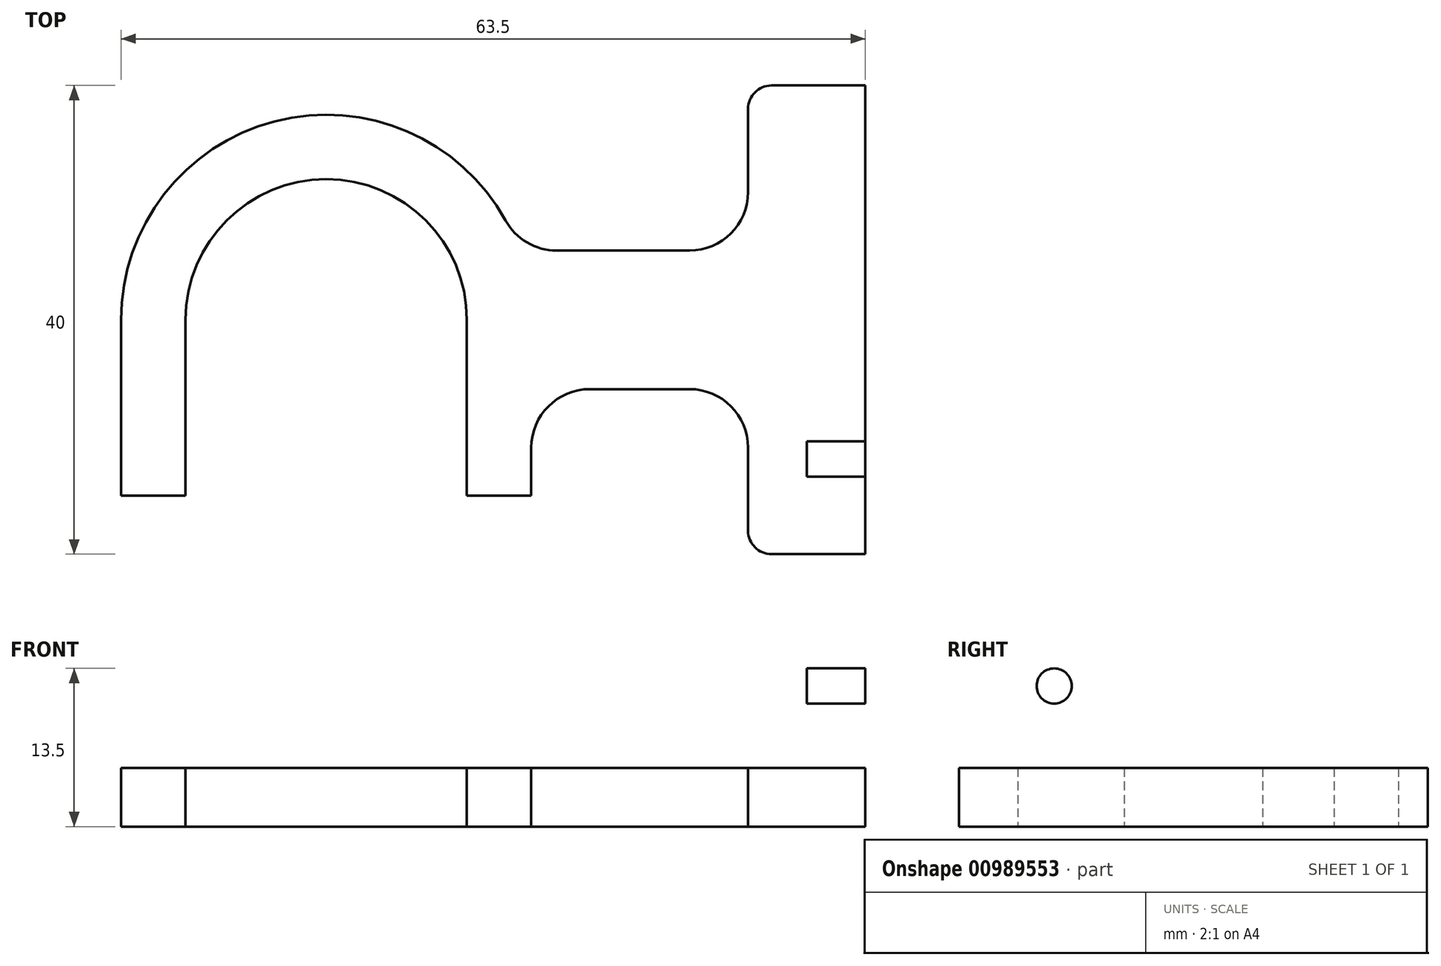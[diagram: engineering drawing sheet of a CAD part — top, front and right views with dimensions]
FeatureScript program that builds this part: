
annotation { "Feature Type Name" : "Feature", "Feature Type Description" : "" }
export const myFeature = defineFeature(function(context is Context, id is Id, definition is map)
    precondition{}
    {
        {
            var Q0;
            Q0=qCreatedBy(makeId("Top.planeOp"),FACE);
            var sketch = newSketch(context, id + "F0", { "sketchPlane" : qUnion([Q0])});
            skLineSegment(sketch, "E0", {"start": v(12, 0) * mm, "end": v(46, 0) * mm, "construction": true});
            skLineSegment(sketch, "E1", {"start": v(36, 10.91) * mm, "end": v(36, 18) * mm});
            skLineSegment(sketch, "E2", {"start": v(38, 20) * mm, "end": v(46, 20) * mm});
            skLineSegment(sketch, "E3", {"start": v(46, 20) * mm, "end": v(46, 0) * mm});
            skLineSegment(sketch, "E4.MirrorCS", {"start": v(36, -10.91) * mm, "end": v(36, -18) * mm});
            skLineSegment(sketch, "E5.MirrorCS", {"start": v(38, -20) * mm, "end": v(46, -20) * mm});
            skLineSegment(sketch, "E6.MirrorCS", {"start": v(46, -20) * mm, "end": v(46, 0) * mm});
            skPoint(sketch, "E7.visualSharp", {"position": v(36, 5.91) * mm});
            skArc(sketch, "E7.filletArc", {"start": v(31, 5.91) * mm, "mid": v(34.54, 7.37) * mm, "end": v(36, 10.91) * mm});
            skArc(sketch, "E8.MirrorCS", {"start": v(31, -5.91) * mm, "mid": v(34.54, -7.37) * mm, "end": v(36, -10.91) * mm});
            skPoint(sketch, "E9.orphan", {"position": v(36, -5.91) * mm});
            skPoint(sketch, "E10.visualSharp", {"position": v(36, 20) * mm});
            skArc(sketch, "E10.filletArc", {"start": v(38, 20) * mm, "mid": v(36.59, 19.41) * mm, "end": v(36, 18) * mm});
            skPoint(sketch, "E11.visualSharp", {"position": v(36, -20) * mm});
            skArc(sketch, "E11.filletArc", {"start": v(36, -18) * mm, "mid": v(36.59, -19.41) * mm, "end": v(38, -20) * mm});
            skArc(sketch, "E12", {"start": v(12, 0) * mm, "mid": v(0, 12) * mm, "end": v(-12, 0) * mm});
            skArc(sketch, "E13", {"start": v(15.3, 8.49) * mm, "mid": v(-4.38, 16.94) * mm, "end": v(-17.5, 0) * mm});
            skLineSegment(sketch, "E14", {"start": v(31, 5.91) * mm, "end": v(19.68, 5.91) * mm});
            skLineSegment(sketch, "E15", {"start": v(31, -5.91) * mm, "end": v(22.5, -5.91) * mm});
            skLineSegment(sketch, "E16", {"start": v(12, 0) * mm, "end": v(12, -15) * mm});
            skLineSegment(sketch, "E17", {"start": v(-12, 0) * mm, "end": v(-12, -15) * mm});
            skLineSegment(sketch, "E18", {"start": v(-17.5, 0) * mm, "end": v(-17.5, -15) * mm});
            skLineSegment(sketch, "E19", {"start": v(17.5, -10.91) * mm, "end": v(17.5, -15) * mm});
            skLineSegment(sketch, "E20", {"start": v(12, -15) * mm, "end": v(17.5, -15) * mm});
            skLineSegment(sketch, "E21.trimOffspring", {"start": v(-12, -15) * mm, "end": v(-17.5, -15) * mm});
            skPoint(sketch, "E22.newPointB", {"position": v(17.5, 0) * mm});
            skArc(sketch, "E22.filletArc", {"start": v(22.5, -5.91) * mm, "mid": v(18.96, -7.37) * mm, "end": v(17.5, -10.91) * mm});
            skArc(sketch, "E23.filletArc", {"start": v(15.3, 8.49) * mm, "mid": v(17.14, 6.6) * mm, "end": v(19.68, 5.91) * mm});
            skSolve(sketch);
        }
        {
            var Q0;
            Q0=makeQuery(id+"F0.imprint","IMPRINT",FACE,{"disambiguationData":[TD([[makeQuery(id+"F0.imprint","IMPRINT",EDGE,{"derivedFrom":sQuery(id+"F0.wireOp",EDGE,"E1")}),-1.0]])]});
            extrude(context, id + "F1", {"entities" : qUnion([Q0]), "depth" : 5 * mm, "offsetDistance" : 25 * mm});
        }
        {
            var Q0;
            Q0=makeQuery(id+"F1.opExtrude","CAP_FACE",FACE,{"disambiguationData":[OSD([sQuery(id+"F0.wireOp",EDGE,"8GoCG5PU-HMSi-upqe-bQzh-JhpqWkjr83KI"),sQuery(id+"F0.wireOp",EDGE,"6tSREIWh-PCzu-5Fpg-hHSP-1HsGlxRufVVe"),sQuery(id+"F0.wireOp",EDGE,"E1"),sQuery(id+"F0.wireOp",EDGE,"E2"),sQuery(id+"F0.wireOp",EDGE,"E3"),sQuery(id+"F0.wireOp",EDGE,"6c7d7d15-5ab0-4980-99c8-1d9f464195fa0.MirrorCS"),sQuery(id+"F0.wireOp",EDGE,"E4.MirrorCS"),sQuery(id+"F0.wireOp",EDGE,"E5.MirrorCS"),sQuery(id+"F0.wireOp",EDGE,"E6.MirrorCS"),sQuery(id+"F0.wireOp",EDGE,"4b4e5443-fceb-4e8f-891c-267329df489d.filletArc"),sQuery(id+"F0.wireOp",EDGE,"E7.filletArc"),sQuery(id+"F0.wireOp",EDGE,"f6371bfa-6fd3-4287-8063-b7b2dde3479b0.MirrorCS"),sQuery(id+"F0.wireOp",EDGE,"E8.MirrorCS"),sQuery(id+"F0.wireOp",EDGE,"E10.filletArc"),sQuery(id+"F0.wireOp",EDGE,"E11.filletArc"),sQuery(id+"F0.wireOp",EDGE,"j99mnrsG-8fU8-ieAR-sIlP-IDkVLY8FqcVX"),sQuery(id+"F0.wireOp",EDGE,"e8211b01-7222-4893-8a72-a379b8b1651b.filletArc"),sQuery(id+"F0.wireOp",EDGE,"3d5b7bb5-eaf6-46b8-ad04-4672c3b9e5740.MirrorCS"),sQuery(id+"F0.wireOp",EDGE,"d1ffaaae-a754-4f0a-98e9-f6a03d5876740.MirrorCS"),sQuery(id+"F0.wireOp",EDGE,"7b9e766f-8db9-407e-a57f-f296288e7c8c.trimOffspring"),sQuery(id+"F0.wireOp",EDGE,"2bcb20b7-2aad-45c3-abd7-b2b32656667b.trimOffspring")])],"isStart":false});
            var sketch = newSketch(context, id + "F2", { "sketchPlane" : qUnion([Q0])});
            skLineSegment(sketch, "E24.bottom", {"start": v(46, 20) * mm, "end": v(41, 20) * mm});
            skLineSegment(sketch, "E24.top", {"start": v(46, -20) * mm, "end": v(41, -20) * mm});
            skLineSegment(sketch, "E24.left", {"start": v(46, 20) * mm, "end": v(46, -20) * mm});
            skLineSegment(sketch, "E24.right", {"start": v(41, 20) * mm, "end": v(41, -20) * mm});
            skSolve(sketch);
        }
        {
            var Q0;
            Q0=makeQuery(id+"F2.imprint","IMPRINT",FACE,{"disambiguationData":[TD([[makeQuery(id+"F2.imprint","IMPRINT",EDGE,{"derivedFrom":sQuery(id+"F2.wireOp",EDGE,"E24.bottom")}),-1.0]])]});
            extrude(context, id + "F3", {"entities" : qUnion([Q0]), "operationType" : NewBodyOperationType.ADD, "depth" : 12 * mm, "offsetDistance" : 25 * mm});
        }
        {
            var Q0;
            Q0=makeQuery(id+"F3.opExtrude","CAP_EDGE",EDGE,{"disambiguationData":[OSD([sQuery(id+"F2.wireOp",EDGE,"E24.right")])],"isStart":true});
            var Q1;
            Q1=makeQuery(id+"F3.opExtrude","CAP_EDGE",EDGE,{"disambiguationData":[OSD([sQuery(id+"F2.wireOp",EDGE,"E24.bottom")])],"isStart":false});
            var Q2;
            Q2=makeQuery(id+"F3.opExtrude","CAP_EDGE",EDGE,{"disambiguationData":[OSD([sQuery(id+"F2.wireOp",EDGE,"E24.top")])],"isStart":false});
            fillet(context, id + "F4", {"entities" : qUnion([Q0, Q1, Q2]), "radius" : 3 * mm, "tangentPropagation" : true, "allowEdgeOverflow" : false});
        }
        {
            var Q0;
            Q0=makeQuery(id+"F3.opExtrude","SWEPT_FACE",FACE,{"disambiguationData":[OSD([sQuery(id+"F2.wireOp",EDGE,"E24.right")])]});
            var sketch = newSketch(context, id + "F5", { "sketchPlane" : qUnion([Q0])});
            skLineSegment(sketch, "E25", {"start": v(-20, 12) * mm, "end": v(20, 12) * mm, "construction": true});
            skLineSegment(sketch, "E26", {"start": v(0, 17) * mm, "end": v(0, 12) * mm, "construction": true});
            skCircle(sketch, "E27", {"center": v(-11.88, 12) * mm, "radius": 1.5 * mm});
            skCircle(sketch, "E28.MirrorC", {"center": v(11.88, 12) * mm, "radius": 1.5 * mm});
            skSolve(sketch);
        }
        {
            var Q0;
            Q0=makeQuery(id+"F5.imprint","IMPRINT",FACE,{"disambiguationData":[TD([[makeQuery(id+"F5.imprint","IMPRINT",EDGE,{"derivedFrom":sQuery(id+"F5.wireOp",EDGE,"E27")}),1.0]])]});
            var Q1;
            Q1=makeQuery(id+"F5.imprint","IMPRINT",FACE,{"disambiguationData":[TD([[makeQuery(id+"F5.imprint","IMPRINT",EDGE,{"derivedFrom":sQuery(id+"F5.wireOp",EDGE,"E28.MirrorC")}),-1.0]])]});
            extrude(context, id + "F6", {"entities" : qUnion([Q0, Q1]), "operationType" : NewBodyOperationType.REMOVE, "oppositeDirection" : true, "depth" : 10 * mm, "offsetDistance" : 25 * mm});
        }
    });
